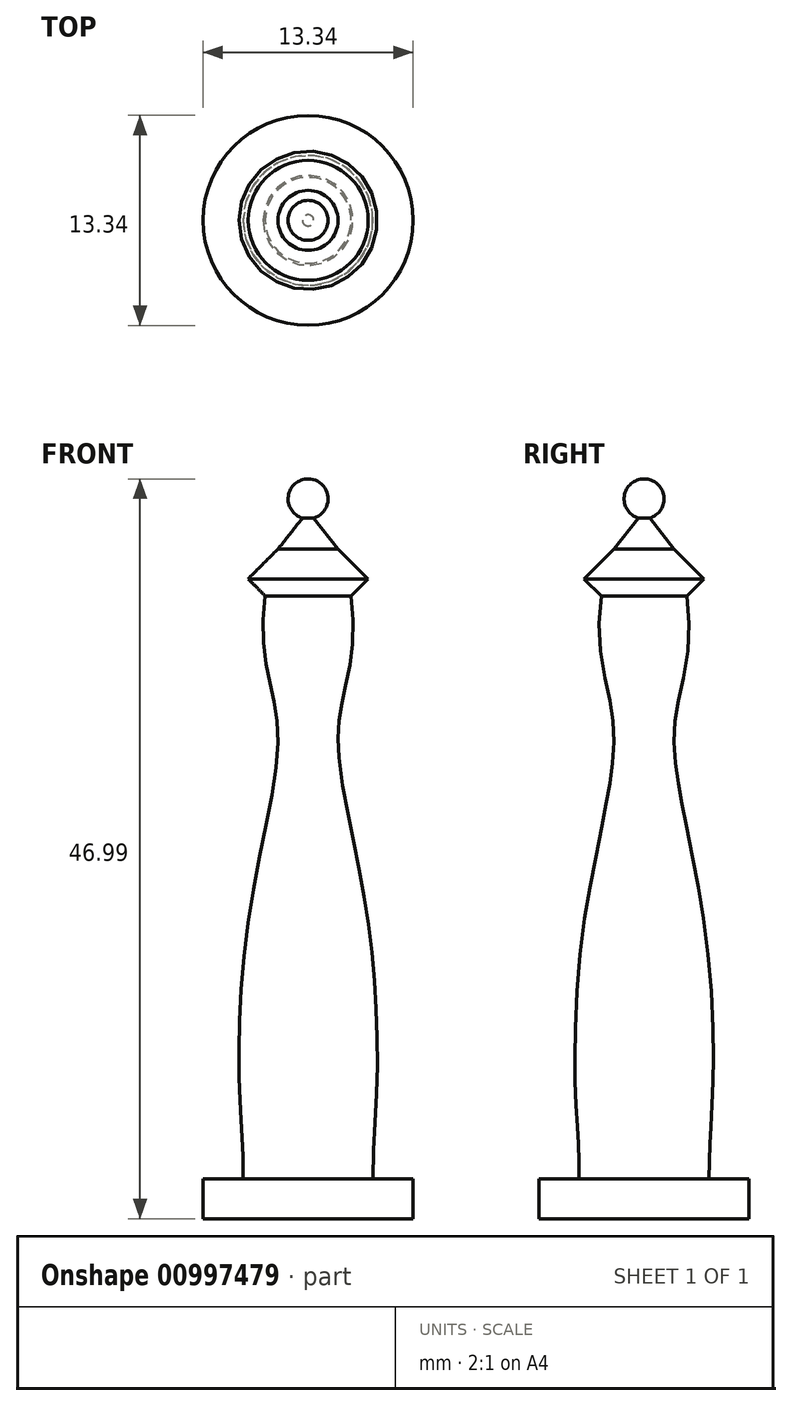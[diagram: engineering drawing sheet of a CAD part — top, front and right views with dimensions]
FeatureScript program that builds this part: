
annotation { "Feature Type Name" : "Feature", "Feature Type Description" : "" }
export const myFeature = defineFeature(function(context is Context, id is Id, definition is map)
    precondition{}
    {
        {
            var Q0;
            Q0=qCreatedBy(makeId("Front.planeOp"),FACE);
            var sketch = newSketch(context, id + "F0", { "sketchPlane" : qUnion([Q0])});
            skLineSegment(sketch, "E0", {"start": v(0, 0) * mm, "end": v(0, 44.45) * mm});
            skPoint(sketch, "E1", {"position": v(0, 41.91) * mm});
            skArc(sketch, "E2", {"start": v(0.36, 41.96) * mm, "mid": v(1.26, 43.36) * mm, "end": v(0, 44.45) * mm});
            skLineSegment(sketch, "E3", {"start": v(1.9, 40) * mm, "end": v(3.81, 38.1) * mm});
            skFitSpline(sketch, "E4", {"points": [v(1.9, 40) * mm, v(2.71, 33.03) * mm, v(1.9, 28) * mm, v(3.8, 16.35) * mm, v(4.34, 4.98) * mm, v(4.13, 0) * mm], "startDerivative": vector(15.58, -35.45) * mm, "endDerivative": vector(0, -39.85) * mm});
            skLineSegment(sketch, "E5", {"start": v(4.13, 0) * mm, "end": v(6.67, 0) * mm});
            skLineSegment(sketch, "E6", {"start": v(6.67, 0) * mm, "end": v(6.67, -2.54) * mm});
            skLineSegment(sketch, "E7", {"start": v(6.67, -2.54) * mm, "end": v(0, -2.54) * mm});
            skLineSegment(sketch, "E8", {"start": v(0, -2.54) * mm, "end": v(0, 0) * mm});
            skLineSegment(sketch, "E9", {"start": v(3.81, 38.1) * mm, "end": v(2.72, 37.01) * mm});
            skLineSegment(sketch, "E10", {"start": v(1.9, 40) * mm, "end": v(0.36, 41.96) * mm});
            skSolve(sketch);
        }
        {
            var Q0;
            Q0 = qSketchRegion(id + "F0", true);
            var Q1;
            Q1=sQuery(id+"F0.wireOp",EDGE,"E0");
            revolve(context, id + "F1", {"surfaceOperationType" : NewSurfaceOperationType.NEW, "entities" : qUnion([Q0]), "axis" : qUnion([Q1]), "revolveType" : RevolveType.FULL});
        }
    });
